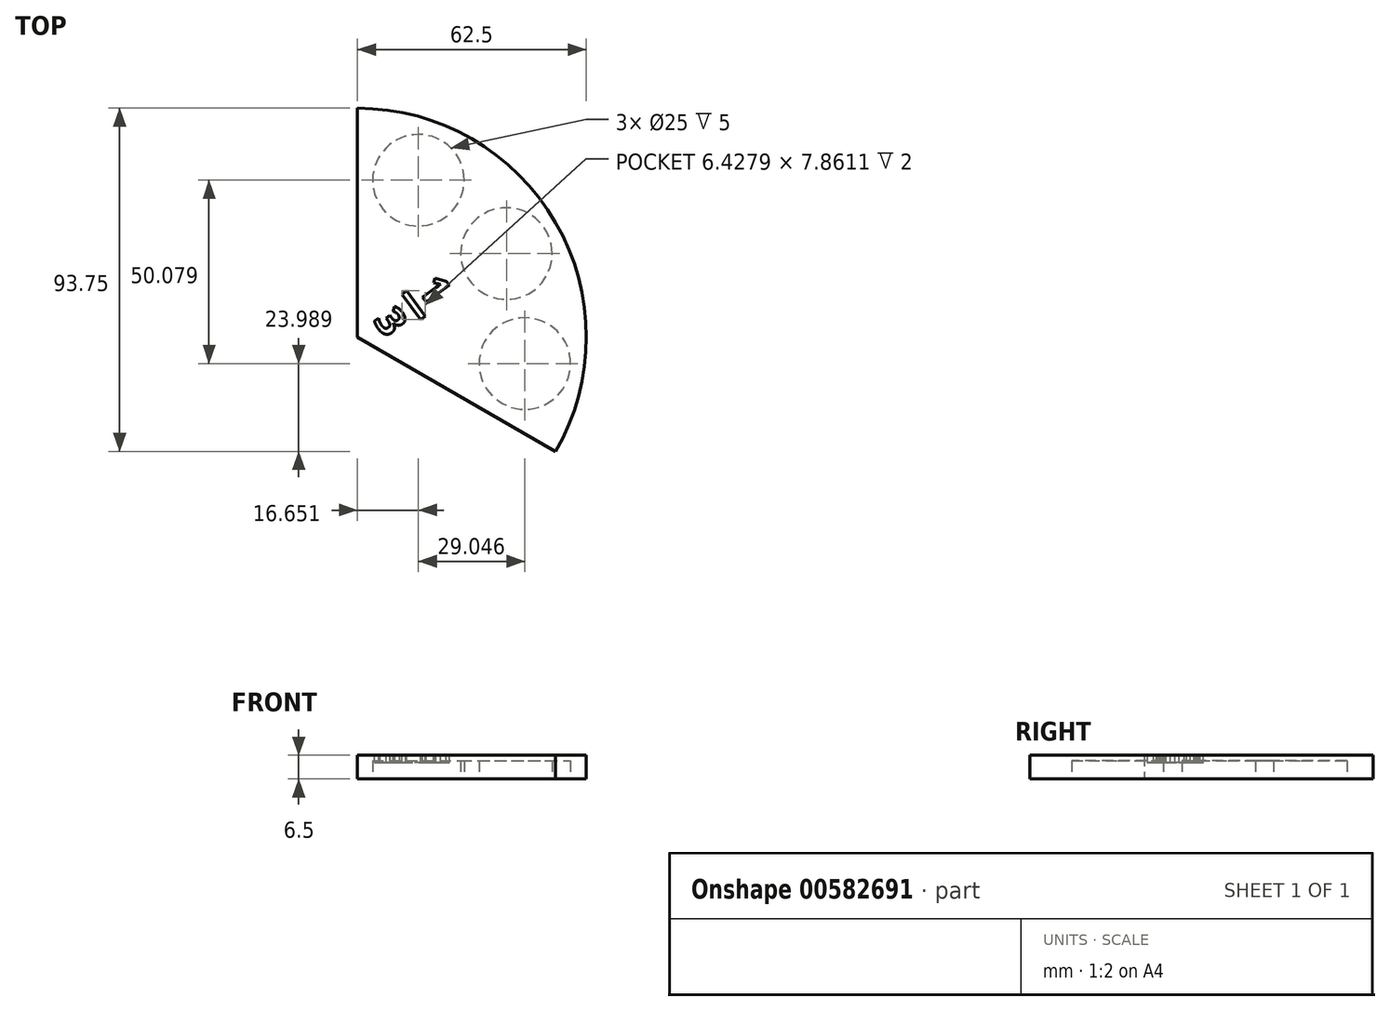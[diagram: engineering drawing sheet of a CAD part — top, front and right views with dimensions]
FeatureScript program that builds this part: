
annotation { "Feature Type Name" : "Feature", "Feature Type Description" : "" }
export const myFeature = defineFeature(function(context is Context, id is Id, definition is map)
    precondition{}
    {
        {
            var Q0;
            Q0=qCreatedBy(makeId("Top.planeOp"),FACE);
            var sketch = newSketch(context, id + "F0", { "sketchPlane" : qUnion([Q0])});
            skArc(sketch, "E0", {"start": v(54.13, -31.25) * mm, "mid": v(54.13, 31.25) * mm, "end": v(0, 62.5) * mm});
            skLineSegment(sketch, "E1", {"start": v(0, 62.5) * mm, "end": v(0, 0) * mm});
            skLineSegment(sketch, "E2", {"start": v(0, 0) * mm, "end": v(54.13, -31.25) * mm});
            skSolve(sketch);
        }
        {
            var Q0;
            Q0=makeQuery(id+"F0.imprint","IMPRINT",FACE,{"disambiguationData":[TD([[makeQuery(id+"F0.imprint","IMPRINT",EDGE,{"derivedFrom":sQuery(id+"F0.wireOp",EDGE,"E0")}),1.0]])]});
            extrude(context, id + "F1", {"entities" : qUnion([Q0]), "depth" : 6.5 * mm, "offsetDistance" : 25 * mm});
        }
        {
            var Q0;
            Q0=makeQuery(id+"F1.opExtrude","CAP_FACE",FACE,{"disambiguationData":[OSD([sQuery(id+"F0.wireOp",EDGE,"E0"),sQuery(id+"F0.wireOp",EDGE,"E1"),sQuery(id+"F0.wireOp",EDGE,"E2")])],"isStart":true});
            var sketch = newSketch(context, id + "F2", { "sketchPlane" : qUnion([Q0])});
            skCircle(sketch, "E3", {"center": v(16.65, -42.82) * mm, "radius": 12.5 * mm});
            skCircle(sketch, "E4", {"center": v(45.7, 7.26) * mm, "radius": 12.5 * mm});
            skCircle(sketch, "E5", {"center": v(40.69, -22.79) * mm, "radius": 12.5 * mm});
            skSolve(sketch);
        }
        {
            var Q0;
            Q0=makeQuery(id+"F2.imprint","IMPRINT",FACE,{"disambiguationData":[TD([[makeQuery(id+"F2.imprint","IMPRINT",EDGE,{"derivedFrom":sQuery(id+"F2.wireOp",EDGE,"E4")}),1.0]])]});
            var Q1;
            Q1=makeQuery(id+"F2.imprint","IMPRINT",FACE,{"disambiguationData":[TD([[makeQuery(id+"F2.imprint","IMPRINT",EDGE,{"derivedFrom":sQuery(id+"F2.wireOp",EDGE,"E5")}),1.0]])]});
            var Q2;
            Q2=makeQuery(id+"F2.imprint","IMPRINT",FACE,{"disambiguationData":[TD([[makeQuery(id+"F2.imprint","IMPRINT",EDGE,{"derivedFrom":sQuery(id+"F2.wireOp",EDGE,"E3")}),1.0]])]});
            extrude(context, id + "F3", {"entities" : qUnion([Q0, Q1, Q2]), "operationType" : NewBodyOperationType.REMOVE, "oppositeDirection" : true, "depth" : 5 * mm, "offsetDistance" : 25 * mm});
        }
        {
            var Q0;
            Q0=makeQuery(id+"F1.opExtrude","CAP_FACE",FACE,{"disambiguationData":[OSD([sQuery(id+"F0.wireOp",EDGE,"E0"),sQuery(id+"F0.wireOp",EDGE,"E1"),sQuery(id+"F0.wireOp",EDGE,"E2")])],"isStart":false});
            var sketch = newSketch(context, id + "F4", { "sketchPlane" : qUnion([Q0])});
            skText(sketch, "E6", { "text": "1\n3", "fontName": "OpenSans-Bold.ttf"});
            const initialGuessF4  = {"E6": [0.01614, 0.0132, 0.58607, -0.81026, 0.00783]};
            skSetInitialGuess(sketch, initialGuessF4);
            skSolve(sketch);
        }
        {
            var Q0;
            Q0 = qSketchRegion(id + "F4", true);
            extrude(context, id + "F5", {"entities" : qUnion([Q0]), "operationType" : NewBodyOperationType.REMOVE, "oppositeDirection" : true, "depth" : 2 * mm, "offsetDistance" : 25 * mm});
        }
        {
            var Q0;
            Q0=makeQuery(id+"F1.opExtrude","CAP_FACE",FACE,{"disambiguationData":[OSD([sQuery(id+"F0.wireOp",EDGE,"E0"),sQuery(id+"F0.wireOp",EDGE,"E1"),sQuery(id+"F0.wireOp",EDGE,"E2")])],"isStart":false});
            var sketch = newSketch(context, id + "F6", { "sketchPlane" : qUnion([Q0])});
            skLineSegment(sketch, "E7", {"start": v(12.12, 11.6) * mm, "end": v(17.22, 4.73) * mm});
            skLineSegment(sketch, "E8", {"start": v(17.22, 4.73) * mm, "end": v(18.55, 5.71) * mm});
            skLineSegment(sketch, "E9", {"start": v(18.55, 5.71) * mm, "end": v(13.45, 12.59) * mm});
            skLineSegment(sketch, "E10", {"start": v(12.12, 11.6) * mm, "end": v(13.45, 12.59) * mm});
            skSolve(sketch);
        }
        {
            var Q0;
            Q0=makeQuery(id+"F6.imprint","IMPRINT",FACE,{"disambiguationData":[TD([[makeQuery(id+"F6.imprint","IMPRINT",EDGE,{"derivedFrom":sQuery(id+"F6.wireOp",EDGE,"E7")}),1.0]])]});
            extrude(context, id + "F7", {"entities" : qUnion([Q0]), "operationType" : NewBodyOperationType.REMOVE, "oppositeDirection" : true, "depth" : 2 * mm, "offsetDistance" : 25 * mm});
        }
    });
